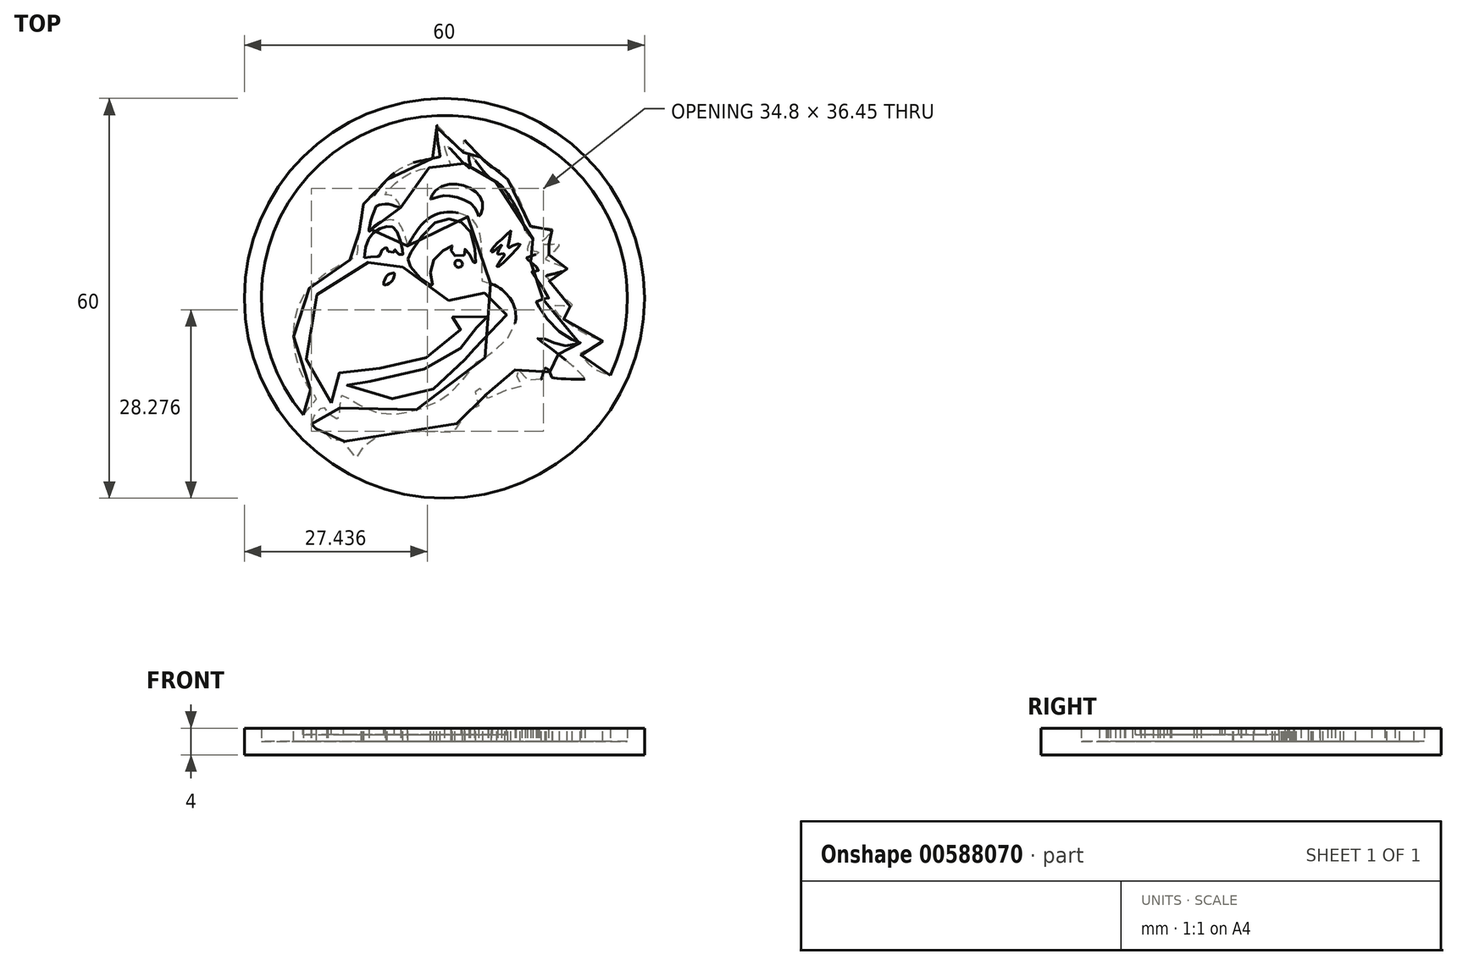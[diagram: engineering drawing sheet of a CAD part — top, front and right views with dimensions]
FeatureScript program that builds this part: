
annotation { "Feature Type Name" : "Feature", "Feature Type Description" : "" }
export const myFeature = defineFeature(function(context is Context, id is Id, definition is map)
    precondition{}
    {
        {
            var Q0;
            Q0=qCreatedBy(makeId("Top.planeOp"),FACE);
            var sketch = newSketch(context, id + "F0", { "sketchPlane" : qUnion([Q0])});
            skCircle(sketch, "E0", {"center": v(0, 0) * mm, "radius": 30 * mm});
            skCircle(sketch, "E1", {"center": v(0, 0) * mm, "radius": 27.45 * mm});
            skSolve(sketch);
        }
        {
            var Q0;
            Q0=qCreatedBy(makeId("Top.planeOp"),FACE);
            var sketch = newSketch(context, id + "F1", { "sketchPlane" : qUnion([Q0])});
            skFitSpline(sketch, "E2", {"points": [v(-16.43, -17.03) * mm, v(-21.1, -9.93) * mm, v(-20.78, -0.97) * mm, v(-15.74, 4.45) * mm, v(-11.82, 5.82) * mm, v(-8.02, 6.07) * mm, v(-6.21, 5.82) * mm, v(-6.03, 5.2) * mm, v(-4.66, 3.14) * mm, v(-1.54, 1.21) * mm, v(2.75, 0.96) * mm, v(5.93, 1.71) * mm, v(9.41, 0) * mm, v(9.72, -2.77) * mm, v(8.48, -5.95) * mm, v(5.93, -8.19) * mm, v(3.87, -9.25) * mm, v(1.38, -12.67) * mm, v(-3.48, -15.47) * mm, v(-9.14, -16.28) * mm, v(-13.37, -14.91) * mm, v(-15.43, -13.54) * mm, v(-15.99, -13.67) * mm, v(-16.43, -17.03) * mm]});
            skSolve(sketch);
        }
        {
            var Q0;
            Q0=qCreatedBy(makeId("Top.planeOp"),FACE);
            var sketch = newSketch(context, id + "F2", { "sketchPlane" : qUnion([Q0])});
            skFitSpline(sketch, "E3", {"points": [v(-21.15, -17.5) * mm, v(-19.22, -15.2) * mm, v(-19.28, -14.82) * mm, v(-21.33, -11.58) * mm, v(-22.58, -4.23) * mm, v(-20.77, 0.87) * mm, v(-16.98, 4.3) * mm, v(-13.24, 6.29) * mm, v(-13, 6.79) * mm, v(-12.8, 9.77) * mm, v(-12.24, 12.14) * mm, v(-12.3, 12.2) * mm, v(-12.24, 13.95) * mm, v(-10.81, 15.25) * mm, v(-10.69, 15.32) * mm, v(-7.39, 18.93) * mm, v(-2.47, 20.86) * mm, v(-0.66, 21.3) * mm, v(-0.66, 21.42) * mm, v(-1.16, 25.9) * mm, v(-1.04, 25.9) * mm, v(2.7, 21.98) * mm, v(2.89, 21.92) * mm, v(2.95, 23.72) * mm, v(3.01, 23.72) * mm, v(6.68, 19.99) * mm, v(7.56, 19.49) * mm, v(9.98, 17.18) * mm, v(12.72, 11.14) * mm, v(13.16, 10.58) * mm, v(14.78, 10.52) * mm, v(16.15, 10.46) * mm, v(15.34, 9.15) * mm, v(14.53, 8.4) * mm, v(14.65, 8.16) * mm, v(16.83, 8.22) * mm, v(17.27, 8.22) * mm, v(16.58, 7.16) * mm, v(15.15, 6.1) * mm, v(15.4, 5.67) * mm, v(18.33, 4.54) * mm, v(18.2, 4.23) * mm, v(15.34, 3.42) * mm, v(15.28, 3.36) * mm, v(16.9, 1.18) * mm, v(19.2, -1.12) * mm, v(18.89, -1.25) * mm, v(16.33, -1.18) * mm, v(17.02, -2.37) * mm, v(22.37, -5.91) * mm, v(23.74, -6.41) * mm, v(22.75, -7.28) * mm, v(20.38, -8.28) * mm, v(20.63, -8.65) * mm, v(22.75, -10.77) * mm, v(25.11, -11.83) * mm, v(22.62, -16.87) * mm, v(14.03, -24.53) * mm, v(6.12, -28.14) * mm, v(-3.4, -28.4) * mm, v(-13.8, -24.78) * mm, v(-20.71, -19.61) * mm, v(-21.15, -17.5) * mm]});
            skFitSpline(sketch, "E4", {"points": [v(-19.96, -18.55) * mm, v(-18.47, -16.44) * mm, v(-18.16, -16.31) * mm, v(-17.22, -17.37) * mm, v(-15.85, -18.12) * mm, v(-15.8, -18) * mm, v(-15.42, -14.63) * mm, v(-15.23, -14.5) * mm, v(-10.38, -17.06) * mm, v(-3.59, -16.56) * mm, v(1.33, -13.76) * mm, v(4.88, -9.59) * mm, v(5, -9.53) * mm, v(9.49, -5.98) * mm, v(10.36, -0.93) * mm, v(7.37, 2.05) * mm, v(5.81, 2.5) * mm, v(5.69, 2.74) * mm, v(5.44, 8.9) * mm, v(3.94, 11.95) * mm, v(0.96, 12.95) * mm, v(-2.72, 11.7) * mm, v(-5.2, 8.4) * mm, v(-5.58, 7.84) * mm, v(-5.58, 8.16) * mm, v(-6.27, 10.27) * mm, v(-7.32, 11.64) * mm, v(-9.82, 11.33) * mm, v(-11.12, 10.15) * mm, v(-11.3, 10.09) * mm, v(-10.38, 13.51) * mm, v(-9.94, 13.95) * mm, v(-8.07, 14.07) * mm, v(-6.58, 13.57) * mm, v(-6.64, 13.88) * mm, v(-7.82, 15.38) * mm, v(-8.88, 15.57) * mm, v(-8.88, 15.63) * mm, v(-4.65, 18.99) * mm, v(0.9, 19.86) * mm, v(0.9, 20.3) * mm, v(0, 23.04) * mm, v(0.64, 22.66) * mm, v(3.82, 19.55) * mm, v(3.82, 20.17) * mm, v(3.7, 21.48) * mm, v(4, 21.42) * mm, v(6.62, 18.24) * mm, v(8.37, 17.06) * mm, v(11.42, 12.27) * mm, v(12.23, 10.02) * mm, v(12.29, 9.84) * mm, v(13.28, 8.97) * mm, v(13.16, 8.97) * mm, v(12.41, 7.28) * mm, v(12.6, 7.22) * mm, v(14.1, 6.91) * mm, v(13.97, 6.72) * mm, v(12.16, 5.98) * mm, v(12.6, 5.73) * mm, v(14.22, 4.23) * mm, v(13.97, 4.17) * mm, v(12.97, 3.92) * mm, v(13.1, 3.86) * mm, v(15.65, 0) * mm, v(15.53, 0) * mm, v(13.84, -0.5) * mm, v(13.84, -0.69) * mm, v(16.65, -4.48) * mm, v(20.38, -6.66) * mm, v(20.5, -6.66) * mm, v(17.9, -7.1) * mm, v(15.09, -6.1) * mm, v(13.97, -6.04) * mm, v(14.03, -6.1) * mm, v(18.14, -9.21) * mm, v(21.07, -12.08) * mm, v(20.82, -12.14) * mm, v(16.2, -11.9) * mm, v(15.96, -11.46) * mm, v(15.15, -10.46) * mm, v(14.6, -12.08) * mm, v(14.47, -12.14) * mm, v(12.85, -12.45) * mm, v(11.3, -10.83) * mm, v(10.6, -10.7) * mm, v(11.17, -12.2) * mm, v(11.6, -13.14) * mm, v(10.6, -13.32) * mm, v(6.56, -15) * mm, v(6.56, -14.76) * mm, v(4.63, -13.2) * mm, v(4.57, -13.82) * mm, v(5.13, -16.06) * mm, v(4.88, -16.25) * mm, v(1.95, -18.62) * mm, v(1.52, -20.23) * mm, v(1.33, -20.23) * mm, v(-2.4, -19.99) * mm, v(-9.57, -20.6) * mm, v(-12.3, -22.48) * mm, v(-13.18, -23.97) * mm, v(-13.3, -23.78) * mm, v(-13.8, -23.35) * mm, v(-14.6, -21.73) * mm, v(-16.17, -21.23) * mm, v(-16.98, -21.23) * mm, v(-17.66, -20.8) * mm, v(-17.47, -20.17) * mm, v(-17.85, -19.92) * mm, v(-18.28, -20.05) * mm, v(-18.66, -19.99) * mm, v(-19.65, -19.24) * mm, v(-19.96, -18.55) * mm]});
            skFitSpline(sketch, "E5", {"points": [v(-12.03, 6.1) * mm, v(-12, 6.29) * mm, v(-11.63, 8.3) * mm, v(-10.04, 10.29) * mm, v(-8.18, 10.78) * mm, v(-7.05, 9.92) * mm, v(-6.22, 6.78) * mm, v(-6.24, 6.6) * mm, v(-6.84, 6.6) * mm, v(-6.98, 6.7) * mm, v(-7.4, 7.3) * mm, v(-7.45, 7.3) * mm, v(-7.6, 6.94) * mm, v(-8.68, 7.25) * mm, v(-8.6, 7.64) * mm, v(-8.83, 7.62) * mm, v(-9.49, 7.04) * mm, v(-9.75, 6.29) * mm, v(-10.04, 6.29) * mm, v(-12.03, 6.1) * mm]});
            skFitSpline(sketch, "E6", {"points": [v(-5.46, 5.86) * mm, v(-5.33, 6.29) * mm, v(-1.87, 11) * mm, v(1.64, 11.78) * mm, v(3.94, 9.92) * mm, v(4.7, 5.42) * mm, v(4.6, 5.1) * mm, v(4.36, 5.47) * mm, v(3.6, 6.9) * mm, v(3.13, 7.35) * mm, v(3.08, 7.35) * mm, v(2.97, 6.52) * mm, v(1.54, 6.4) * mm, v(1, 7.05) * mm, v(1.2, 7.82) * mm, v(1.18, 7.89) * mm, v(-0.33, 7.02) * mm, v(-2.04, 4.59) * mm, v(-1.7, 2) * mm, v(-1.62, 1.87) * mm, v(-2.57, 2.22) * mm, v(-5.18, 4.94) * mm, v(-5.46, 5.86) * mm]});
            skFitSpline(sketch, "E7", {"points": [v(1.77, 5.62) * mm, v(1.56, 5.27) * mm, v(1.88, 4.68) * mm, v(2.58, 4.84) * mm, v(2.62, 5.43) * mm, v(2.14, 5.7) * mm, v(1.77, 5.62) * mm]});
            skFitSpline(sketch, "E8", {"points": [v(-16.95, -15.67) * mm, v(-17.02, -15.82) * mm, v(-20.84, -8.79) * mm, v(-18.98, 0.73) * mm, v(-11.91, 5.32) * mm, v(-6.77, 5.58) * mm, v(-6.66, 5.43) * mm, v(-2.55, 0.69) * mm, v(3.52, 0) * mm, v(5.67, 0.76) * mm, v(6.6, 0.62) * mm, v(9.04, -1.3) * mm, v(8.74, -3.98) * mm, v(4.3, -7.64) * mm, v(2.75, -8.16) * mm, v(2.67, -8.53) * mm, v(3, -9) * mm, v(2.82, -9.57) * mm, v(-0.77, -13.12) * mm, v(-4.1, -14.27) * mm, v(-8.88, -15.08) * mm, v(-14.1, -13.3) * mm, v(-15.13, -12.64) * mm, v(-14.54, -12.49) * mm, v(-8.99, -12.27) * mm, v(-2.58, -10.45) * mm, v(1.04, -8.64) * mm, v(3.38, -6.16) * mm, v(3.82, -4.75) * mm, v(5.08, -4.3) * mm, v(7.04, -2.6) * mm, v(7.23, -2.42) * mm, v(5.93, -2.94) * mm, v(3.04, -3.01) * mm, v(1, -2.86) * mm, v(1.3, -3.27) * mm, v(2.41, -4.12) * mm, v(2.56, -4.35) * mm, v(0.71, -6.83) * mm, v(-3.66, -9.23) * mm, v(-8.5, -10.3) * mm, v(-14.32, -11.05) * mm, v(-15.8, -11.2) * mm, v(-16.84, -13.08) * mm, v(-16.95, -15.67) * mm]});
            skFitSpline(sketch, "E9", {"points": [v(-9.01, 1.99) * mm, v(-9.1, 2.3) * mm, v(-8.46, 3.5) * mm, v(-7.58, 3.8) * mm, v(-7.5, 3.77) * mm, v(-7.54, 3.26) * mm, v(-7.91, 2.54) * mm, v(-9.01, 1.99) * mm]});
            skFitSpline(sketch, "E10", {"points": [v(5.14, 12.3) * mm, v(5.1, 12.37) * mm, v(4.66, 13.5) * mm, v(2.68, 14.9) * mm, v(0.4, 15.42) * mm, v(-1.13, 15.17) * mm, v(-2.02, 14.86) * mm, v(-2.04, 14.92) * mm, v(-1.65, 15.85) * mm, v(0.55, 17.07) * mm, v(2.91, 16.91) * mm, v(4.81, 15.88) * mm, v(5.76, 14.23) * mm, v(5.43, 12.6) * mm, v(5.14, 12.3) * mm]});
            skFitSpline(sketch, "E11", {"points": [v(7.03, 6.95) * mm, v(7.03, 7.2) * mm, v(7.08, 7.28) * mm, v(7.8, 8.18) * mm, v(8.87, 9.07) * mm, v(9.96, 10.14) * mm, v(9.96, 9.83) * mm, v(9.56, 7.84) * mm, v(9.56, 7.58) * mm, v(9.73, 7.6) * mm, v(10.76, 8.12) * mm, v(11.34, 8.14) * mm, v(11.3, 7.95) * mm, v(8.9, 5.42) * mm, v(8, 4.7) * mm, v(7.89, 4.74) * mm, v(8.09, 5.22) * mm, v(8.74, 6.11) * mm, v(9.08, 6.64) * mm, v(8, 6.6) * mm], "startDerivative": vector(-0.6, 9.84) * mm, "endDerivative": vector(-24, -3.84) * mm});
            skFitSpline(sketch, "E12", {"points": [v(7.03, 6.95) * mm, v(7.3, 7.02) * mm, v(7.97, 7.56) * mm, v(8.6, 7.98) * mm, v(8.57, 7.88) * mm, v(8.14, 7.22) * mm, v(7.98, 6.75) * mm, v(8, 6.6) * mm], "startDerivative": vector(2.24, 0.25) * mm, "endDerivative": vector(0.26, -1.62) * mm});
            skSolve(sketch);
        }
        {
            var Q0;
            Q0=makeQuery(id+"F0.imprint","IMPRINT",FACE,{"disambiguationData":[TD([[makeQuery(id+"F0.imprint","IMPRINT",EDGE,{"derivedFrom":sQuery(id+"F0.wireOp",EDGE,"E1")}),1.0]])]});
            var Q1;
            Q1=makeQuery(id+"F0.imprint","IMPRINT",FACE,{"disambiguationData":[TD([[makeQuery(id+"F0.imprint","IMPRINT",EDGE,{"derivedFrom":sQuery(id+"F0.wireOp",EDGE,"E0")}),1.0]])]});
            extrude(context, id + "F3", {"entities" : qUnion([Q0, Q1]), "depth" : 2 * mm, "offsetDistance" : 25 * mm});
        }
        {
            var Q0;
            Q0=makeQuery(id+"F0.imprint","IMPRINT",FACE,{"disambiguationData":[TD([[makeQuery(id+"F0.imprint","IMPRINT",EDGE,{"derivedFrom":sQuery(id+"F0.wireOp",EDGE,"E0")}),1.0]])]});
            var Q1;
            Q1 = qSketchRegion(id + "F2", true);
            var Q2;
            Q2=makeQuery(id+"F2.imprint","IMPRINT",FACE,{"disambiguationData":[TD([[makeQuery(id+"F2.imprint","IMPRINT",EDGE,{"derivedFrom":sQuery(id+"F2.wireOp",EDGE,"E9")}),-1.0]])]});
            var Q3;
            Q3=makeQuery(id+"F2.imprint","IMPRINT",FACE,{"disambiguationData":[TD([[makeQuery(id+"F2.imprint","IMPRINT",EDGE,{"derivedFrom":sQuery(id+"F2.wireOp",EDGE,"E10")}),-1.0]])]});
            var Q4;
            Q4=makeQuery(id+"F2.imprint","IMPRINT",FACE,{"disambiguationData":[TD([[makeQuery(id+"F2.imprint","IMPRINT",EDGE,{"derivedFrom":sQuery(id+"F2.wireOp",EDGE,"E11")}),-1.0]])]});
            extrude(context, id + "F4", {"entities" : qUnion([Q0, Q1, Q2, Q3, Q4]), "operationType" : NewBodyOperationType.ADD, "depth" : 4 * mm, "offsetDistance" : 25 * mm});
        }
        {
            var Q0;
            Q0 = qSketchRegion(id + "F1", true);
            extrude(context, id + "F5", {"entities" : qUnion([Q0]), "operationType" : NewBodyOperationType.ADD, "depth" : 3 * mm, "offsetDistance" : 25 * mm});
        }
    });
